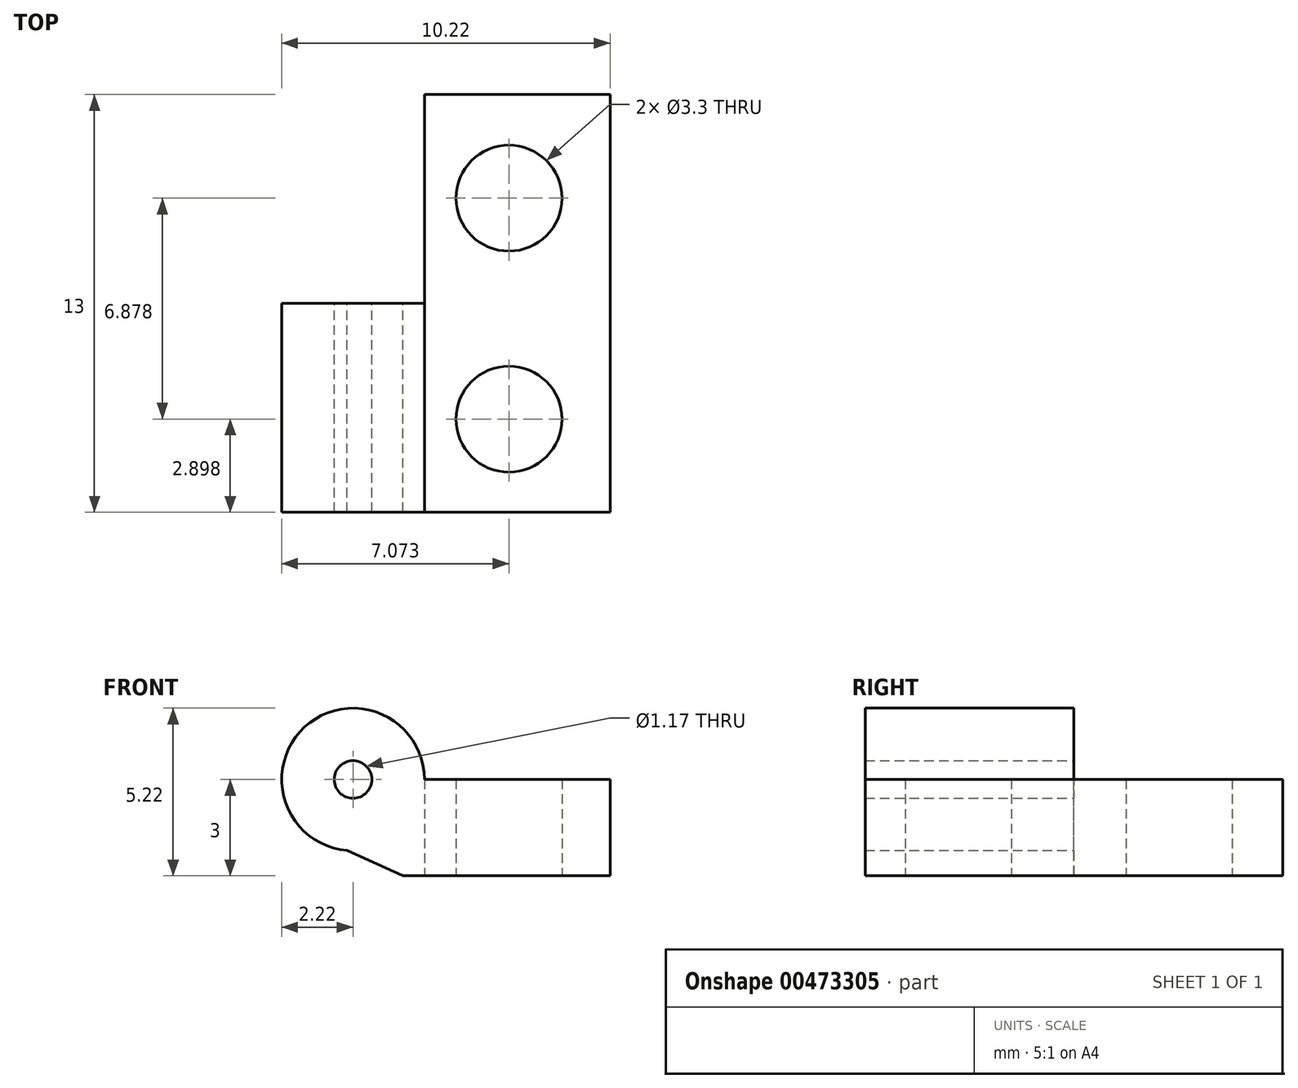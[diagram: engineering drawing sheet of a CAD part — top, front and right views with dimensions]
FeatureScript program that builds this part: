
annotation { "Feature Type Name" : "Feature", "Feature Type Description" : "" }
export const myFeature = defineFeature(function(context is Context, id is Id, definition is map)
    precondition{}
    {
        {
            var Q0;
            Q0=qCreatedBy(makeId("Top.planeOp"),FACE);
            var sketch = newSketch(context, id + "F0", { "sketchPlane" : qUnion([Q0])});
            skLineSegment(sketch, "E0.bottom", {"start": v(0, 0) * mm, "end": v(16, 0) * mm});
            skLineSegment(sketch, "E0.top", {"start": v(0, 13) * mm, "end": v(16, 13) * mm});
            skLineSegment(sketch, "E0.left", {"start": v(0, 0) * mm, "end": v(0, 13) * mm});
            skLineSegment(sketch, "E0.right", {"start": v(16, 0) * mm, "end": v(16, 13) * mm});
            skCircle(sketch, "E1", {"center": v(3.12, 9.78) * mm, "radius": 1.65 * mm});
            skCircle(sketch, "E2", {"center": v(12.85, 9.78) * mm, "radius": 1.65 * mm});
            skCircle(sketch, "E3", {"center": v(3.12, 2.9) * mm, "radius": 1.65 * mm});
            skCircle(sketch, "E4", {"center": v(12.85, 2.9) * mm, "radius": 1.65 * mm});
            skSolve(sketch);
        }
        {
            var Q0;
            Q0=qSketchRegion(id+"F0",true);
            extrude(context, id + "F1", {"entities" : qUnion([Q0]), "depth" : 3 * mm, "offsetDistance" : 25 * mm});
        }
        {
            var Q0;
            Q0=makeQuery(id+"F1.opExtrude","SWEPT_FACE",FACE,{"disambiguationData":[OSD([sQuery(id+"F0.wireOp",EDGE,"E0.top")])]});
            var sketch = newSketch(context, id + "F2", { "sketchPlane" : qUnion([Q0])});
            skCircle(sketch, "E5", {"center": v(-8, 3) * mm, "radius": 2.22 * mm});
            skSolve(sketch);
        }
        {
            var Q0;
            Q0=qSketchRegion(id+"F2",true);
            var Q1;
            Q1=makeQuery(id+"F1.opExtrude","SWEPT_FACE",FACE,{"disambiguationData":[OSD([sQuery(id+"F0.wireOp",EDGE,"E0.bottom")])]});
            extrude(context, id + "F3", {"entities" : qUnion([Q0]), "operationType" : NewBodyOperationType.ADD, "endBound" : BoundingType.UP_TO_SURFACE, "oppositeDirection" : true, "depth" : 25 * mm, "endBoundEntityFace" : qUnion([Q1]), "offsetDistance" : 25 * mm});
        }
        {
            var Q0;
            Q0=makeQuery(id+"F3.boolean.opBoolean","MERGE",FACE,{"derivedFrom":[makeQuery(id+"F1.opExtrude","SWEPT_FACE",FACE,{"disambiguationData":[OSD([sQuery(id+"F0.wireOp",EDGE,"E0.top")])]}),makeQuery(id+"F3.opExtrude","CAP_FACE",FACE,{"disambiguationData":[OSD([sQuery(id+"F2.wireOp",EDGE,"E5")])],"isStart":true})]});
            var sketch = newSketch(context, id + "F4", { "sketchPlane" : qUnion([Q0])});
            skCircle(sketch, "E6", {"center": v(-8, 3) * mm, "radius": 0.58 * mm});
            skLineSegment(sketch, "E7", {"start": v(-9.55, 0) * mm, "end": v(-8, 0.9) * mm});
            skLineSegment(sketch, "E8", {"start": v(-8, 0.9) * mm, "end": v(-6.45, 0) * mm});
            skLineSegment(sketch, "E9", {"start": v(-9.55, 0) * mm, "end": v(-6.45, 0) * mm});
            skSolve(sketch);
        }
        {
            var Q0;
            Q0=qSketchRegion(id+"F4",true);
            extrude(context, id + "F5", {"entities" : qUnion([Q0]), "operationType" : NewBodyOperationType.REMOVE, "oppositeDirection" : true, "depth" : 25 * mm, "offsetDistance" : 25 * mm});
        }
        {
            var Q0;
            Q0=makeQuery(id+"F3.boolean.opBoolean","MERGE",FACE,{"derivedFrom":[makeQuery(id+"F1.opExtrude","SWEPT_FACE",FACE,{"disambiguationData":[OSD([sQuery(id+"F0.wireOp",EDGE,"E0.top")])]}),makeQuery(id+"F3.opExtrude","CAP_FACE",FACE,{"disambiguationData":[OSD([sQuery(id+"F2.wireOp",EDGE,"E5")])],"isStart":true})]});
            var sketch = newSketch(context, id + "F6", { "sketchPlane" : qUnion([Q0])});
            skArc(sketch, "E10", {"start": v(-8.19, 0.79) * mm, "mid": v(-6.5, 1.37) * mm, "end": v(-5.78, 3) * mm});
            skLineSegment(sketch, "E11", {"start": v(-9.55, 0) * mm, "end": v(-8.19, 0.79) * mm});
            skLineSegment(sketch, "E12", {"start": v(-5.78, 3) * mm, "end": v(0, 3) * mm});
            skLineSegment(sketch, "E13", {"start": v(0, 3) * mm, "end": v(0, -1.07) * mm});
            skLineSegment(sketch, "E14", {"start": v(0, -1.07) * mm, "end": v(-9.55, 0) * mm});
            skSolve(sketch);
        }
        {
            var Q0;
            Q0=qSketchRegion(id+"F6",true);
            extrude(context, id + "F7", {"entities" : qUnion([Q0]), "operationType" : NewBodyOperationType.REMOVE, "oppositeDirection" : true, "depth" : 25 * mm, "offsetDistance" : 25 * mm});
        }
        {
            var Q0;
            Q0=makeQuery(id+"F3.boolean.opBoolean","MERGE",FACE,{"derivedFrom":[makeQuery(id+"F1.opExtrude","SWEPT_FACE",FACE,{"disambiguationData":[OSD([sQuery(id+"F0.wireOp",EDGE,"E0.top")])]}),makeQuery(id+"F3.opExtrude","CAP_FACE",FACE,{"disambiguationData":[OSD([sQuery(id+"F2.wireOp",EDGE,"E5")])],"isStart":true})]});
            var sketch = newSketch(context, id + "F8", { "sketchPlane" : qUnion([Q0])});
            skLineSegment(sketch, "E15", {"start": v(-9.55, 0) * mm, "end": v(-7.81, 0.79) * mm});
            skLineSegment(sketch, "E16", {"start": v(-7.81, 0.79) * mm, "end": v(-8, 0.9) * mm});
            skLineSegment(sketch, "E17", {"start": v(-8, 0.9) * mm, "end": v(-9.55, 0) * mm});
            skSolve(sketch);
        }
        {
            var Q0;
            Q0=qSketchRegion(id+"F8",true);
            var Q1;
            {var subQ0=sQuery(id+"F0.wireOp",EDGE,"E0.bottom");Q1=makeQuery(id+"F3.boolean.opBoolean","MERGE",FACE,{"derivedFrom":[makeQuery(id+"F1.opExtrude","SWEPT_FACE",FACE,{"disambiguationData":[OSD([subQ0])]}),makeQuery(id+"F3.opExtrude","CAP_FACE",FACE,{"disambiguationData":[OSD([subQ0])],"isStart":false})]});}
            extrude(context, id + "F9", {"entities" : qUnion([Q0]), "operationType" : NewBodyOperationType.ADD, "endBound" : BoundingType.UP_TO_SURFACE, "oppositeDirection" : true, "depth" : 25 * mm, "endBoundEntityFace" : qUnion([Q1]), "offsetDistance" : 25 * mm});
        }
        {
            var Q0;
            {var subQ0=sQuery(id+"F0.wireOp",EDGE,"E2");var subQ1=sQuery(id+"F0.wireOp",EDGE,"E0.top");var subQ3=sQuery(id+"F0.wireOp",EDGE,"E0.right");var subQ4=sQuery(id+"F0.wireOp",EDGE,"E0.bottom");var subQ5=sQuery(id+"F0.wireOp",EDGE,"E4");Q0=makeQuery(id+"F3.boolean.opBoolean","SPLIT",FACE,{"disambiguationData":[TD([makeQuery(id+"F1.opExtrude","SWEPT_FACE",FACE,{"disambiguationData":[OSD([subQ3])]})])],"derivedFrom":makeQuery(id+"F1.opExtrude","CAP_FACE",FACE,{"disambiguationData":[OSD([subQ4,subQ1,sQuery(id+"F0.wireOp",EDGE,"E0.left"),subQ3,sQuery(id+"F0.wireOp",EDGE,"E1"),subQ0,sQuery(id+"F0.wireOp",EDGE,"E3"),subQ5])],"isStart":false})});}
            var sketch = newSketch(context, id + "F10", { "sketchPlane" : qUnion([Q0])});
            skLineSegment(sketch, "E18.bottom", {"start": v(10.22, 6.5) * mm, "end": v(2.43, 6.5) * mm});
            skLineSegment(sketch, "E18.top", {"start": v(10.22, 15.15) * mm, "end": v(2.43, 15.15) * mm});
            skLineSegment(sketch, "E18.left", {"start": v(10.22, 6.5) * mm, "end": v(10.22, 15.15) * mm});
            skLineSegment(sketch, "E18.right", {"start": v(2.43, 6.5) * mm, "end": v(2.43, 15.15) * mm});
            skSolve(sketch);
        }
        {
            var Q0;
            Q0=qSketchRegion(id+"F10",true);
            extrude(context, id + "F11", {"entities" : qUnion([Q0]), "operationType" : NewBodyOperationType.REMOVE, "oppositeDirection" : true, "depth" : 25 * mm, "offsetDistance" : 25 * mm, "hasSecondDirection" : true, "secondDirectionOppositeDirection" : false, "secondDirectionDepth" : 25 * mm});
        }
    });
